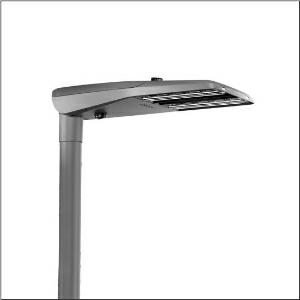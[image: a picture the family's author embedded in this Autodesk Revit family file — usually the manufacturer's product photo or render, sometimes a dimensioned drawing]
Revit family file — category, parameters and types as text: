
# Revit family: streetlight_sl_11_iq_midi___st0_5st0_5_5xc3h51y08me_12eb
name_source: partatom
category: Lighting Fixtures
units: mm (PartAtom-declared; Revit-internal decimal feet)

## family parameters
Cut with Voids When Loaded = No
Host = Face
Light Source = No
Part Type = Normal
Room Calculation Point = No
Round Connector Dimension = Use Diameter
Shared = No

## types (1)
- --- (1 x LED, 17940 lm, 122.7 W, 3000K)
    Apparent Load = 123 VA
    CIE Flux Codes = 43 74 97 100 100
    Color Rendering = 70
    Color Temperature = 3000K
    Default Elevation = 1800 mm
    Description = Streetlight SL 11 iQ midi, mast luminaire, primary light control with 3 zone facetted reflector, of plastic, silver coated, highly specular, primary optical cover: cover, of PMMA, transparent, light distribution: ST0.5ST0.5, light emission: direct distribution, primary light characteristic: asymmetric, installation type: post-top, side-entry, LED, High Power LED, rated luminous flux: 17.940lm, luminous efficacy: 146lm/W, light colour: 730, colour temperature: 3000K, control: presetting dimming logarithmic, Street-Remote, Auto-Match, Temp-Guard, Lumen-Switch, Night-Set, Smart-Wire, Light-Fading, Desk-Remote (wireless, voltage-free reading and setting of iQ features in the workshop via application-optimized NFC function/RFID function), optimised constant luminous flux control (CLO 2.0), with cable H07RN-F 5x 1.5mm², mains connection: 220..240V, AC, 50/60Hz, connection cable pre-assembled, cable length: 12,5m, start of lifetime: 123W, end of service life: 130W, reduction: 56W, luminaire housing, of diecast aluminium, powder-coated, Siteco® metallic grey (DB 702S), please order mast flange separately, inclination adjustable without tools: 0°, 5°, 10°, 15° (post-top) | 0°, -5°, -10°, -15° (side-entry), sealing non-destructively replaceable, multi-level sealing system, length: 780mm, width: 376mm, height: 118mm, spigot size: 60/76mm (post-top) and 42/60/76mm (side-entry), mast flange for spigot size: 42mm: 5XC10008XM4, 60mm: 5XC10008XM2, 76/60mm: 5XC10108XM1, equipment: Power, Smart Interface below and above, protection rating (complete): IP66, insulation class (complete): insulation class II (safety insulation), certification: CE, ENEC in preparation, impact resistance: IK09, permissible operating ambient temperature for outdoor applications: -25..+50°C, standard-compliant lighting for roads and squares, packaging unit: 1 piece

Light Distribution: ST0.5ST0.5
    Height = 118 mm
    Lamp = 1 x LED
    Lamp Light Flux = 17940 lm
    Lamp Power = 122.7 W
    Lamp count = 1
    Length = 780 mm
    Luminous efficacy = 146 lm/W
    Manufacturer = Siteco
    ModVariant = No
    Model = 5XC3H51Y08ME
    Number of Poles = 1
    OnlyDefault = Yes
    Power Factor = 1
    Product Name = Streetlight SL 11 iQ midi | ST0.5ST0.5
    Product group = mast luminaire | pylon top
    ProductGroupID = 6100
    Protection Class = Protection class II
    Protection Degree = IP 66
    RLX_Detail_Level = 1
    RlxData = <blob elided: 74481 chars, md5=706f6422>
    Socket = socket
    Standby Power = 0 W
    System Light Flux = 17940 lm
    System Power = 123 W
    Type Comments = factory setting: luminous flux: 100 % | dim-lin: 254 | 553 mA
    Type Image = l_1004429.jpg
    URL = http://relux.com
    VarID = @adj_043239
    Voltage = 0 V
    Weight = 0.00 kg
    Width = 376 mm

## geometry (parser evidence)
native form markers: Blend x4, Sweep x12
no freeform markers — native parametric forms only
